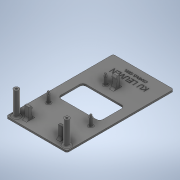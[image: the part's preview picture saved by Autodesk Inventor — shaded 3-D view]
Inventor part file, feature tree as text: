
AUTODESK INVENTOR PART (.ipt)
format: ipt  version: 2022 (Build 260153000, 153)  size: 617,472 bytes
history: native  units: mm
features: sketch x8, extrude x7, fillet x4, plane x2, mirror x1, emboss x1
ambient origin geometry x8: Origin, YZ Plane, XZ Plane, XY Plane, X Axis, Y Axis, Z Axis, Center Point
bodies: Solid1 (feature_tree)
feature tree (23):
  extrude  "Extrusion1"  Depth=127.0mm
  extrude  "Extrusion8"  Depth=4.0mm
  fillet  "Fillet3"  Radius=9.0mm
  extrude  "Extrusion9"  Depth=1.0mm
  fillet  "Fillet4"  Radius=2.5mm
  fillet  "Fillet5"  Radius=2.5mm
  plane  "Work Plane1"
  extrude  "Extrusion11"  Depth=3.0mm
  plane  "Work Plane2"
  mirror  "Mirror1"
  extrude  "Extrusion12"  Depth=2.0mm
  extrude  "Extrusion13"  Depth=29.0mm
  fillet  "Fillet6"  Radius=10.5mm
  extrude  "Extrusion14"  Depth=10.5mm
  emboss  "Emboss2"
  sketch  "Sketch1"  dims[d0=72.0mm d1=127.0mm]
  sketch  "Sketch2"  dims[d2=2.0mm d3=0.0mm d34=4.0mm d62=9.0mm d63=0.0mm]
  sketch  "Sketch8"  dims[d64=1.0mm d65=2.5mm d66=2.5mm d67=2.5mm]
  sketch  "Sketch10"  dims[d68=3.0mm d69=0.0mm d70=0.5mm]
  sketch  "Sketch11"  dims[d82=2.0mm d83=70.0mm]
  sketch  "Sketch12"  dims[d84=82.45mm d85=29.0mm d86=10.5mm]
  sketch  "Sketch13"  dims[d87=25.8mm d88=10.5mm]
  sketch  "Sketch16"  dims[d89=2.3mm d90=11.0mm d91=-16.0mm d92=10.0mm d96=1.0mm d98=3.0mm d100=2.5mm d102=1.5mm d103=3.0mm d105=5.0mm d106=0.0mm d107=10.0mm d109=2.5mm d112=3.0mm d113=3.0mm d115=5.0mm d116=0.0mm d117=10.9mm d118=1.0mm d119=1.5mm d120=10.9mm d121=5.5mm d122=82.45mm d123=27.7mm d124=50.0mm d125=30.0mm d126=50.0mm d127=4.0mm d128=6.0mm d129=6.0mm d130=6.0mm d131=6.0mm d132=6.0mm d133=28.0mm d134=0.0mm d135=2.0mm d136=2.5mm d137=2.5mm d138=10.0mm d139=0.0mm d162=5.0mm d163=1.0mm d164=0.0mm]
